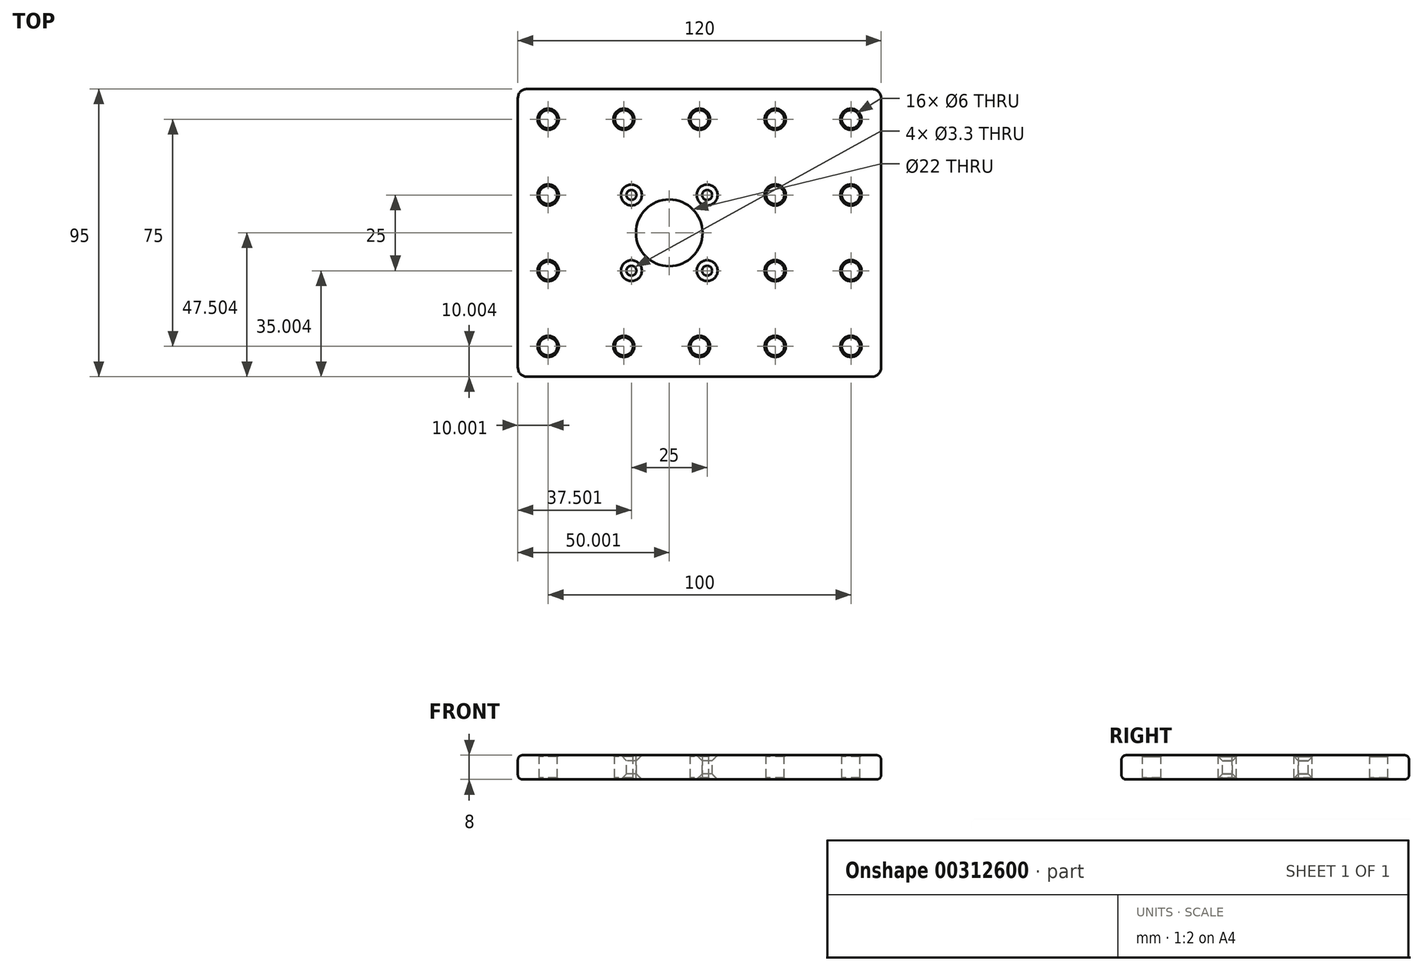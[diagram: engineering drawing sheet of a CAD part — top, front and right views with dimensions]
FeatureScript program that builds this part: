
annotation { "Feature Type Name" : "Feature", "Feature Type Description" : "" }
export const myFeature = defineFeature(function(context is Context, id is Id, definition is map)
    precondition{}
    {
        {
            var Q0;
            Q0=qCreatedBy(makeId("Top.planeOp"),FACE);
            var sketch = newSketch(context, id + "F0", { "sketchPlane" : qUnion([Q0])});
            skLineSegment(sketch, "E0.bottom", {"start": v(-81.17, 39.3) * mm, "end": v(38.83, 39.3) * mm});
            skLineSegment(sketch, "E0.top", {"start": v(-81.17, -55.7) * mm, "end": v(38.83, -55.7) * mm});
            skLineSegment(sketch, "E0.left", {"start": v(-81.17, 39.3) * mm, "end": v(-81.17, -55.7) * mm});
            skLineSegment(sketch, "E0.right", {"start": v(38.83, 39.3) * mm, "end": v(38.83, -55.7) * mm});
            skCircle(sketch, "E1", {"center": v(-18.67, 4.3) * mm, "radius": 1.65 * mm});
            skLineSegment(sketch, "E2", {"start": v(-21.17, 39.3) * mm, "end": v(-21.17, -55.7) * mm, "construction": true});
            skLineSegment(sketch, "E3", {"start": v(-81.17, -8.2) * mm, "end": v(38.83, -8.2) * mm, "construction": true});
            skCircle(sketch, "E4", {"center": v(28.83, 29.3) * mm, "radius": 3 * mm});
            skCircle(sketch, "E5.0.1.0", {"center": v(-18.67, -20.7) * mm, "radius": 1.65 * mm});
            skCircle(sketch, "E5.1.0.0", {"center": v(-43.67, 4.3) * mm, "radius": 1.65 * mm});
            skCircle(sketch, "E5.1.1.0", {"center": v(-43.67, -20.7) * mm, "radius": 1.65 * mm});
            skLineSegment(sketch, "E5.direction1", {"start": v(-18.67, 4.3) * mm, "end": v(-43.67, 4.3) * mm, "construction": true});
            skLineSegment(sketch, "E5.direction2", {"start": v(-18.67, 4.3) * mm, "end": v(-18.67, -20.7) * mm, "construction": true});
            skPoint(sketch, "E6", {"position": v(-31.17, 4.3) * mm});
            skCircle(sketch, "E7", {"center": v(-31.17, -8.2) * mm, "radius": 11 * mm});
            skCircle(sketch, "E8.0.1.0", {"center": v(28.83, 4.3) * mm, "radius": 3 * mm});
            skCircle(sketch, "E8.0.2.0", {"center": v(28.83, -20.7) * mm, "radius": 3 * mm});
            skCircle(sketch, "E8.0.3.0", {"center": v(28.83, -45.7) * mm, "radius": 3 * mm});
            skCircle(sketch, "E8.1.0.0", {"center": v(3.83, 29.3) * mm, "radius": 3 * mm});
            skCircle(sketch, "E8.1.1.0", {"center": v(3.83, 4.3) * mm, "radius": 3 * mm});
            skCircle(sketch, "E8.1.2.0", {"center": v(3.83, -20.7) * mm, "radius": 3 * mm});
            skCircle(sketch, "E8.1.3.0", {"center": v(3.83, -45.7) * mm, "radius": 3 * mm});
            skCircle(sketch, "E8.2.0.0", {"center": v(-21.17, 29.3) * mm, "radius": 3 * mm});
            skCircle(sketch, "E8.2.3.0", {"center": v(-21.17, -45.7) * mm, "radius": 3 * mm});
            skCircle(sketch, "E8.3.0.0", {"center": v(-46.17, 29.3) * mm, "radius": 3 * mm});
            skCircle(sketch, "E8.3.3.0", {"center": v(-46.17, -45.7) * mm, "radius": 3 * mm});
            skLineSegment(sketch, "E8.direction1", {"start": v(28.83, 29.3) * mm, "end": v(3.83, 29.3) * mm, "construction": true});
            skLineSegment(sketch, "E8.direction2", {"start": v(28.83, 29.3) * mm, "end": v(28.83, 4.3) * mm, "construction": true});
            skCircle(sketch, "E9.0.4.0", {"center": v(-71.17, 29.3) * mm, "radius": 3 * mm});
            skCircle(sketch, "E9.0.4.1", {"center": v(-71.17, 4.3) * mm, "radius": 3 * mm});
            skCircle(sketch, "E9.0.4.2", {"center": v(-71.17, -20.7) * mm, "radius": 3 * mm});
            skCircle(sketch, "E9.0.4.3", {"center": v(-71.17, -45.7) * mm, "radius": 3 * mm});
            skSolve(sketch);
        }
        {
            var Q0;
            Q0=makeQuery(id+"F0.imprint","IMPRINT",FACE,{"disambiguationData":[TD([[makeQuery(id+"F0.imprint","IMPRINT",EDGE,{"derivedFrom":sQuery(id+"F0.wireOp",EDGE,"E0.bottom")}),-1.0]])]});
            extrude(context, id + "F1", {"entities" : qUnion([Q0]), "oppositeDirection" : true, "depth" : 8 * mm});
        }
        {
            var Q0;
            Q0=makeQuery(id+"F1.opExtrude","CAP_EDGE",EDGE,{"disambiguationData":[OSD([sQuery(id+"F0.wireOp",EDGE,"E0.top")])],"isStart":true});
            var Q1;
            Q1=makeQuery(id+"F1.opExtrude","CAP_EDGE",EDGE,{"disambiguationData":[OSD([sQuery(id+"F0.wireOp",EDGE,"E0.right")])],"isStart":true});
            var Q2;
            Q2=makeQuery(id+"F1.opExtrude","CAP_EDGE",EDGE,{"disambiguationData":[OSD([sQuery(id+"F0.wireOp",EDGE,"E0.bottom")])],"isStart":true});
            var Q3;
            Q3=makeQuery(id+"F1.opExtrude","CAP_EDGE",EDGE,{"disambiguationData":[OSD([sQuery(id+"F0.wireOp",EDGE,"E0.left")])],"isStart":true});
            var Q4;
            Q4=makeQuery(id+"F1.opExtrude","CAP_EDGE",EDGE,{"disambiguationData":[OSD([sQuery(id+"F0.wireOp",EDGE,"E0.top")])],"isStart":false});
            var Q5;
            Q5=makeQuery(id+"F1.opExtrude","CAP_EDGE",EDGE,{"disambiguationData":[OSD([sQuery(id+"F0.wireOp",EDGE,"E0.right")])],"isStart":false});
            var Q6;
            Q6=makeQuery(id+"F1.opExtrude","CAP_EDGE",EDGE,{"disambiguationData":[OSD([sQuery(id+"F0.wireOp",EDGE,"E0.left")])],"isStart":false});
            var Q7;
            Q7=makeQuery(id+"F1.opExtrude","CAP_EDGE",EDGE,{"disambiguationData":[OSD([sQuery(id+"F0.wireOp",EDGE,"E0.bottom")])],"isStart":false});
            fillet(context, id + "F2", {"entities" : qUnion([Q0, Q1, Q2, Q3, Q4, Q5, Q6, Q7]), "radius" : 1.5 * mm, "tangentPropagation" : true, "allowEdgeOverflow" : false});
        }
        {
            var Q0;
            Q0=makeQuery(id+"F1.opExtrude","CAP_EDGE",EDGE,{"disambiguationData":[OSD([sQuery(id+"F0.wireOp",EDGE,"E5.1.0.0")])],"isStart":true});
            var Q1;
            Q1=makeQuery(id+"F1.opExtrude","CAP_EDGE",EDGE,{"disambiguationData":[OSD([sQuery(id+"F0.wireOp",EDGE,"E1")])],"isStart":true});
            var Q2;
            Q2=makeQuery(id+"F1.opExtrude","CAP_EDGE",EDGE,{"disambiguationData":[OSD([sQuery(id+"F0.wireOp",EDGE,"E5.0.1.0")])],"isStart":true});
            var Q3;
            Q3=makeQuery(id+"F1.opExtrude","CAP_EDGE",EDGE,{"disambiguationData":[OSD([sQuery(id+"F0.wireOp",EDGE,"E5.1.1.0")])],"isStart":true});
            var Q4;
            Q4=makeQuery(id+"F1.opExtrude","CAP_EDGE",EDGE,{"disambiguationData":[OSD([sQuery(id+"F0.wireOp",EDGE,"E5.1.1.0")])],"isStart":false});
            var Q5;
            Q5=makeQuery(id+"F1.opExtrude","CAP_EDGE",EDGE,{"disambiguationData":[OSD([sQuery(id+"F0.wireOp",EDGE,"E1")])],"isStart":false});
            var Q6;
            Q6=makeQuery(id+"F1.opExtrude","CAP_EDGE",EDGE,{"disambiguationData":[OSD([sQuery(id+"F0.wireOp",EDGE,"E5.0.1.0")])],"isStart":false});
            var Q7;
            Q7=makeQuery(id+"F1.opExtrude","CAP_EDGE",EDGE,{"disambiguationData":[OSD([sQuery(id+"F0.wireOp",EDGE,"E5.1.0.0")])],"isStart":false});
            chamfer(context, id + "F3", {"entities" : qUnion([Q0, Q1, Q2, Q3, Q4, Q5, Q6, Q7]), "width" : 1.8 * mm, "tangentPropagation" : true});
        }
        {
            var Q0;
            Q0=makeQuery(id+"F1.opExtrude","SWEPT_EDGE",EDGE,{"disambiguationData":[OSD([sQuery(id+"F0.wireOp",EDGE,"E0.top"),sQuery(id+"F0.wireOp",EDGE,"E0.left")])]});
            var Q1;
            Q1=makeQuery(id+"F1.opExtrude","SWEPT_EDGE",EDGE,{"disambiguationData":[OSD([sQuery(id+"F0.wireOp",EDGE,"E0.top"),sQuery(id+"F0.wireOp",EDGE,"E0.right")])]});
            var Q2;
            Q2=makeQuery(id+"F1.opExtrude","SWEPT_EDGE",EDGE,{"disambiguationData":[OSD([sQuery(id+"F0.wireOp",EDGE,"E0.bottom"),sQuery(id+"F0.wireOp",EDGE,"E0.left")])]});
            var Q3;
            Q3=makeQuery(id+"F1.opExtrude","SWEPT_EDGE",EDGE,{"disambiguationData":[OSD([sQuery(id+"F0.wireOp",EDGE,"E0.bottom"),sQuery(id+"F0.wireOp",EDGE,"E0.right")])]});
            fillet(context, id + "F4", {"entities" : qUnion([Q0, Q1, Q2, Q3]), "radius" : 3 * mm, "tangentPropagation" : true, "allowEdgeOverflow" : false});
        }
        {
            var Q0;
            Q0=makeQuery(id+"F1.opExtrude","CAP_EDGE",EDGE,{"disambiguationData":[OSD([sQuery(id+"F0.wireOp",EDGE,"E9.0.4.3")])],"isStart":false});
            var Q1;
            Q1=makeQuery(id+"F1.opExtrude","CAP_EDGE",EDGE,{"disambiguationData":[OSD([sQuery(id+"F0.wireOp",EDGE,"E9.0.4.3")])],"isStart":true});
            var Q2;
            Q2=makeQuery(id+"F1.opExtrude","CAP_EDGE",EDGE,{"disambiguationData":[OSD([sQuery(id+"F0.wireOp",EDGE,"E8.0.3.0")])],"isStart":false});
            var Q3;
            Q3=makeQuery(id+"F1.opExtrude","CAP_EDGE",EDGE,{"disambiguationData":[OSD([sQuery(id+"F0.wireOp",EDGE,"E8.1.3.0")])],"isStart":false});
            var Q4;
            Q4=makeQuery(id+"F1.opExtrude","CAP_EDGE",EDGE,{"disambiguationData":[OSD([sQuery(id+"F0.wireOp",EDGE,"E8.3.3.0")])],"isStart":false});
            var Q5;
            Q5=makeQuery(id+"F1.opExtrude","CAP_EDGE",EDGE,{"disambiguationData":[OSD([sQuery(id+"F0.wireOp",EDGE,"E8.2.3.0")])],"isStart":false});
            var Q6;
            Q6=makeQuery(id+"F1.opExtrude","CAP_EDGE",EDGE,{"disambiguationData":[OSD([sQuery(id+"F0.wireOp",EDGE,"E8.1.3.0")])],"isStart":true});
            var Q7;
            Q7=makeQuery(id+"F1.opExtrude","CAP_EDGE",EDGE,{"disambiguationData":[OSD([sQuery(id+"F0.wireOp",EDGE,"E8.0.3.0")])],"isStart":true});
            var Q8;
            Q8=makeQuery(id+"F1.opExtrude","CAP_EDGE",EDGE,{"disambiguationData":[OSD([sQuery(id+"F0.wireOp",EDGE,"E8.2.3.0")])],"isStart":true});
            var Q9;
            Q9=makeQuery(id+"F1.opExtrude","CAP_EDGE",EDGE,{"disambiguationData":[OSD([sQuery(id+"F0.wireOp",EDGE,"E8.3.3.0")])],"isStart":true});
            var Q10;
            Q10=makeQuery(id+"F1.opExtrude","CAP_EDGE",EDGE,{"disambiguationData":[OSD([sQuery(id+"F0.wireOp",EDGE,"E8.0.1.0")])],"isStart":false});
            var Q11;
            Q11=makeQuery(id+"F1.opExtrude","CAP_EDGE",EDGE,{"disambiguationData":[OSD([sQuery(id+"F0.wireOp",EDGE,"E8.1.1.0")])],"isStart":false});
            var Q12;
            Q12=makeQuery(id+"F1.opExtrude","CAP_EDGE",EDGE,{"disambiguationData":[OSD([sQuery(id+"F0.wireOp",EDGE,"E8.1.2.0")])],"isStart":false});
            var Q13;
            Q13=makeQuery(id+"F1.opExtrude","CAP_EDGE",EDGE,{"disambiguationData":[OSD([sQuery(id+"F0.wireOp",EDGE,"E8.1.1.0")])],"isStart":true});
            var Q14;
            Q14=makeQuery(id+"F1.opExtrude","CAP_EDGE",EDGE,{"disambiguationData":[OSD([sQuery(id+"F0.wireOp",EDGE,"E8.0.2.0")])],"isStart":false});
            var Q15;
            Q15=makeQuery(id+"F1.opExtrude","CAP_EDGE",EDGE,{"disambiguationData":[OSD([sQuery(id+"F0.wireOp",EDGE,"E4")])],"isStart":false});
            var Q16;
            Q16=makeQuery(id+"F1.opExtrude","CAP_EDGE",EDGE,{"disambiguationData":[OSD([sQuery(id+"F0.wireOp",EDGE,"E8.1.2.0")])],"isStart":true});
            var Q17;
            Q17=makeQuery(id+"F1.opExtrude","CAP_EDGE",EDGE,{"disambiguationData":[OSD([sQuery(id+"F0.wireOp",EDGE,"E8.1.0.0")])],"isStart":false});
            var Q18;
            Q18=makeQuery(id+"F1.opExtrude","CAP_EDGE",EDGE,{"disambiguationData":[OSD([sQuery(id+"F0.wireOp",EDGE,"E8.0.1.0")])],"isStart":true});
            var Q19;
            Q19=makeQuery(id+"F1.opExtrude","CAP_EDGE",EDGE,{"disambiguationData":[OSD([sQuery(id+"F0.wireOp",EDGE,"E8.1.0.0")])],"isStart":true});
            var Q20;
            Q20=makeQuery(id+"F1.opExtrude","CAP_EDGE",EDGE,{"disambiguationData":[OSD([sQuery(id+"F0.wireOp",EDGE,"E4")])],"isStart":true});
            var Q21;
            Q21=makeQuery(id+"F1.opExtrude","CAP_EDGE",EDGE,{"disambiguationData":[OSD([sQuery(id+"F0.wireOp",EDGE,"E8.0.2.0")])],"isStart":true});
            var Q22;
            Q22=makeQuery(id+"F1.opExtrude","CAP_EDGE",EDGE,{"disambiguationData":[OSD([sQuery(id+"F0.wireOp",EDGE,"E8.2.0.0")])],"isStart":false});
            var Q23;
            Q23=makeQuery(id+"F1.opExtrude","CAP_EDGE",EDGE,{"disambiguationData":[OSD([sQuery(id+"F0.wireOp",EDGE,"E8.3.0.0")])],"isStart":false});
            var Q24;
            Q24=makeQuery(id+"F1.opExtrude","CAP_EDGE",EDGE,{"disambiguationData":[OSD([sQuery(id+"F0.wireOp",EDGE,"E9.0.4.0")])],"isStart":false});
            var Q25;
            Q25=makeQuery(id+"F1.opExtrude","CAP_EDGE",EDGE,{"disambiguationData":[OSD([sQuery(id+"F0.wireOp",EDGE,"E8.2.0.0")])],"isStart":true});
            var Q26;
            Q26=makeQuery(id+"F1.opExtrude","CAP_EDGE",EDGE,{"disambiguationData":[OSD([sQuery(id+"F0.wireOp",EDGE,"E8.3.0.0")])],"isStart":true});
            var Q27;
            Q27=makeQuery(id+"F1.opExtrude","CAP_EDGE",EDGE,{"disambiguationData":[OSD([sQuery(id+"F0.wireOp",EDGE,"E9.0.4.0")])],"isStart":true});
            var Q28;
            Q28=makeQuery(id+"F1.opExtrude","CAP_EDGE",EDGE,{"disambiguationData":[OSD([sQuery(id+"F0.wireOp",EDGE,"E9.0.4.1")])],"isStart":false});
            var Q29;
            Q29=makeQuery(id+"F1.opExtrude","CAP_EDGE",EDGE,{"disambiguationData":[OSD([sQuery(id+"F0.wireOp",EDGE,"E9.0.4.2")])],"isStart":false});
            var Q30;
            Q30=makeQuery(id+"F1.opExtrude","CAP_EDGE",EDGE,{"disambiguationData":[OSD([sQuery(id+"F0.wireOp",EDGE,"E9.0.4.2")])],"isStart":true});
            var Q31;
            Q31=makeQuery(id+"F1.opExtrude","CAP_EDGE",EDGE,{"disambiguationData":[OSD([sQuery(id+"F0.wireOp",EDGE,"E9.0.4.1")])],"isStart":true});
            chamfer(context, id + "F5", {"entities" : qUnion([Q0, Q1, Q2, Q3, Q4, Q5, Q6, Q7, Q8, Q9, Q10, Q11, Q12, Q13, Q14, Q15, Q16, Q17, Q18, Q19, Q20, Q21, Q22, Q23, Q24, Q25, Q26, Q27, Q28, Q29, Q30, Q31]), "width" : .5 * mm, "tangentPropagation" : true});
        }
    });
